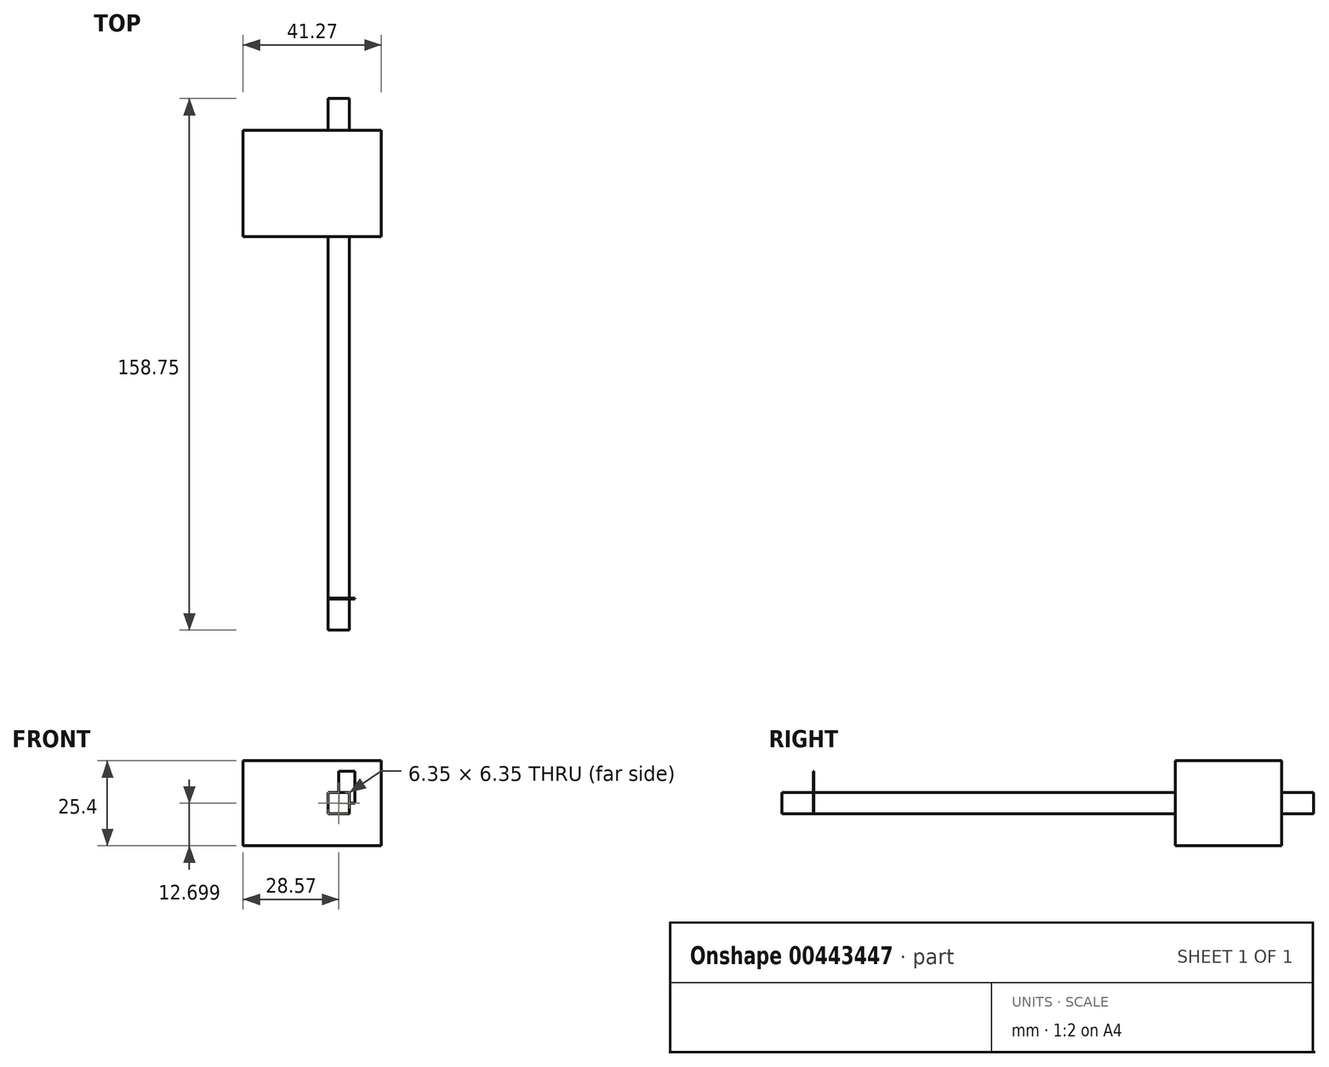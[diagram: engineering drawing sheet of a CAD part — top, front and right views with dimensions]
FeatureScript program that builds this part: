
annotation { "Feature Type Name" : "Feature", "Feature Type Description" : "" }
export const myFeature = defineFeature(function(context is Context, id is Id, definition is map)
    precondition{}
    {
        {
            var Q0;
            Q0=qCreatedBy(makeId("Front.planeOp"),FACE);
            var sketch = newSketch(context, id + "F0", { "sketchPlane" : qUnion([Q0])});
            skLineSegment(sketch, "E0.bottom", {"start": v(0, 5.1) * mm, "end": v(-41.27, 5.1) * mm});
            skLineSegment(sketch, "E0.top", {"start": v(0, 30.5) * mm, "end": v(-41.28, 30.5) * mm});
            skLineSegment(sketch, "E0.left", {"start": v(0, 5.1) * mm, "end": v(0, 30.5) * mm});
            skLineSegment(sketch, "E0.right", {"start": v(-41.27, 5.1) * mm, "end": v(-41.28, 30.5) * mm});
            skSolve(sketch);
        }
        {
            var Q0;
            Q0=makeQuery(id+"F0.imprint","IMPRINT",FACE,{"disambiguationData":[TD([[makeQuery(id+"F0.imprint","IMPRINT",EDGE,{"derivedFrom":sQuery(id+"F0.wireOp",EDGE,"E0.bottom")}),-1.0]])]});
            extrude(context, id + "F1", {"entities" : qUnion([Q0]), "depth" : 31.75 * mm});
        }
        {
            var Q0;
            Q0=makeQuery(id+"F1.opExtrude","CAP_FACE",FACE,{"disambiguationData":[OSD([sQuery(id+"F0.wireOp",EDGE,"E0.bottom"),sQuery(id+"F0.wireOp",EDGE,"E0.top"),sQuery(id+"F0.wireOp",EDGE,"E0.left"),sQuery(id+"F0.wireOp",EDGE,"E0.right")])],"isStart":false});
            var sketch = newSketch(context, id + "F2", { "sketchPlane" : qUnion([Q0])});
            skLineSegment(sketch, "E1.bottom", {"start": v(-9.53, 20.98) * mm, "end": v(-15.88, 20.98) * mm});
            skLineSegment(sketch, "E1.top", {"start": v(-9.52, 14.63) * mm, "end": v(-15.88, 14.63) * mm});
            skLineSegment(sketch, "E1.left", {"start": v(-9.53, 20.98) * mm, "end": v(-9.52, 14.63) * mm});
            skLineSegment(sketch, "E1.right", {"start": v(-15.88, 20.98) * mm, "end": v(-15.88, 14.63) * mm});
            skSolve(sketch);
        }
        {
            var Q0;
            Q0=makeQuery(id+"F2.imprint","IMPRINT",FACE,{"disambiguationData":[TD([[makeQuery(id+"F2.imprint","IMPRINT",EDGE,{"derivedFrom":sQuery(id+"F2.wireOp",EDGE,"E1.bottom")}),1.0]])]});
            extrude(context, id + "F3", {"entities" : qUnion([Q0]), "operationType" : NewBodyOperationType.ADD, "depth" : 107.95 * mm, "hasSecondDirection" : true, "secondDirectionOppositeDirection" : true, "secondDirectionDepth" : 41.27 * mm});
        }
        {
            var Q0;
            Q0=makeQuery(id+"F3.opExtrude","CAP_FACE",FACE,{"disambiguationData":[OSD([sQuery(id+"F2.wireOp",EDGE,"E1.bottom"),sQuery(id+"F2.wireOp",EDGE,"E1.top"),sQuery(id+"F2.wireOp",EDGE,"E1.left"),sQuery(id+"F2.wireOp",EDGE,"E1.right")])],"isStart":false});
            var sketch = newSketch(context, id + "F4", { "sketchPlane" : qUnion([Q0])});
            skLineSegment(sketch, "E2.bottom", {"start": v(-12.7, 27.33) * mm, "end": v(-7.94, 27.33) * mm});
            skLineSegment(sketch, "E2.top", {"start": v(-12.7, 17.8) * mm, "end": v(-7.94, 17.8) * mm});
            skLineSegment(sketch, "E2.left", {"start": v(-12.7, 27.33) * mm, "end": v(-12.7, 17.8) * mm});
            skLineSegment(sketch, "E2.right", {"start": v(-7.94, 27.33) * mm, "end": v(-7.94, 17.8) * mm});
            skLineSegment(sketch, "E3.bottom", {"start": v(-15.88, 20.98) * mm, "end": v(-12.7, 20.98) * mm});
            skLineSegment(sketch, "E3.top", {"start": v(-15.88, 14.63) * mm, "end": v(-12.7, 14.63) * mm});
            skLineSegment(sketch, "E3.left", {"start": v(-15.88, 20.98) * mm, "end": v(-15.88, 14.63) * mm});
            skLineSegment(sketch, "E3.right", {"start": v(-12.7, 20.98) * mm, "end": v(-12.7, 14.63) * mm});
            skSolve(sketch);
        }
        {
            var Q0;
            Q0=makeQuery(id+"F4.imprint","IMPRINT",FACE,{"disambiguationData":[TD([[makeQuery(id+"F4.imprint","IMPRINT",EDGE,{"derivedFrom":sQuery(id+"F4.wireOp",EDGE,"E3.bottom")}),1.0]])]});
            var Q1;
            {var subQ0=sQuery(id+"F4.wireOp",EDGE,"E3.right");Q1=makeQuery(id+"F4.imprint","IMPRINT",FACE,{"disambiguationData":[TD([[makeQuery(id+"F4.imprint","IMPRINT",EDGE,{"derivedFrom":subQ0}),1.0]])]});}
            var Q2;
            {var subQ5=sQuery(id+"F4.wireOp",EDGE,"E2.bottom");Q2=makeQuery(id+"F4.imprint","IMPRINT",FACE,{"disambiguationData":[TD([[makeQuery(id+"F4.imprint","IMPRINT",EDGE,{"derivedFrom":subQ5}),-1.0]])]});}
            extrude(context, id + "F5", {"entities" : qUnion([Q0, Q1, Q2]), "depth" : 0.15 * mm});
        }
        {
            var Q0;
            Q0=makeQuery(id+"F3.opExtrude","CAP_FACE",FACE,{"disambiguationData":[OSD([sQuery(id+"F2.wireOp",EDGE,"E1.bottom"),sQuery(id+"F2.wireOp",EDGE,"E1.top"),sQuery(id+"F2.wireOp",EDGE,"E1.left"),sQuery(id+"F2.wireOp",EDGE,"E1.right")])],"isStart":false});
            var sketch = newSketch(context, id + "F6", { "sketchPlane" : qUnion([Q0])});
            skLineSegment(sketch, "E4.bottom", {"start": v(-15.88, 20.98) * mm, "end": v(-9.52, 20.98) * mm});
            skLineSegment(sketch, "E4.top", {"start": v(-15.88, 14.63) * mm, "end": v(-9.52, 14.63) * mm});
            skLineSegment(sketch, "E4.left", {"start": v(-15.88, 20.98) * mm, "end": v(-15.88, 14.63) * mm});
            skLineSegment(sketch, "E4.right", {"start": v(-9.52, 20.98) * mm, "end": v(-9.52, 14.63) * mm});
            skSolve(sketch);
        }
        {
            var Q0;
            Q0 = qSketchRegion(id + "F6", true);
            extrude(context, id + "F7", {"entities" : qUnion([Q0]), "depth" : 9.52 * mm});
        }
    });
